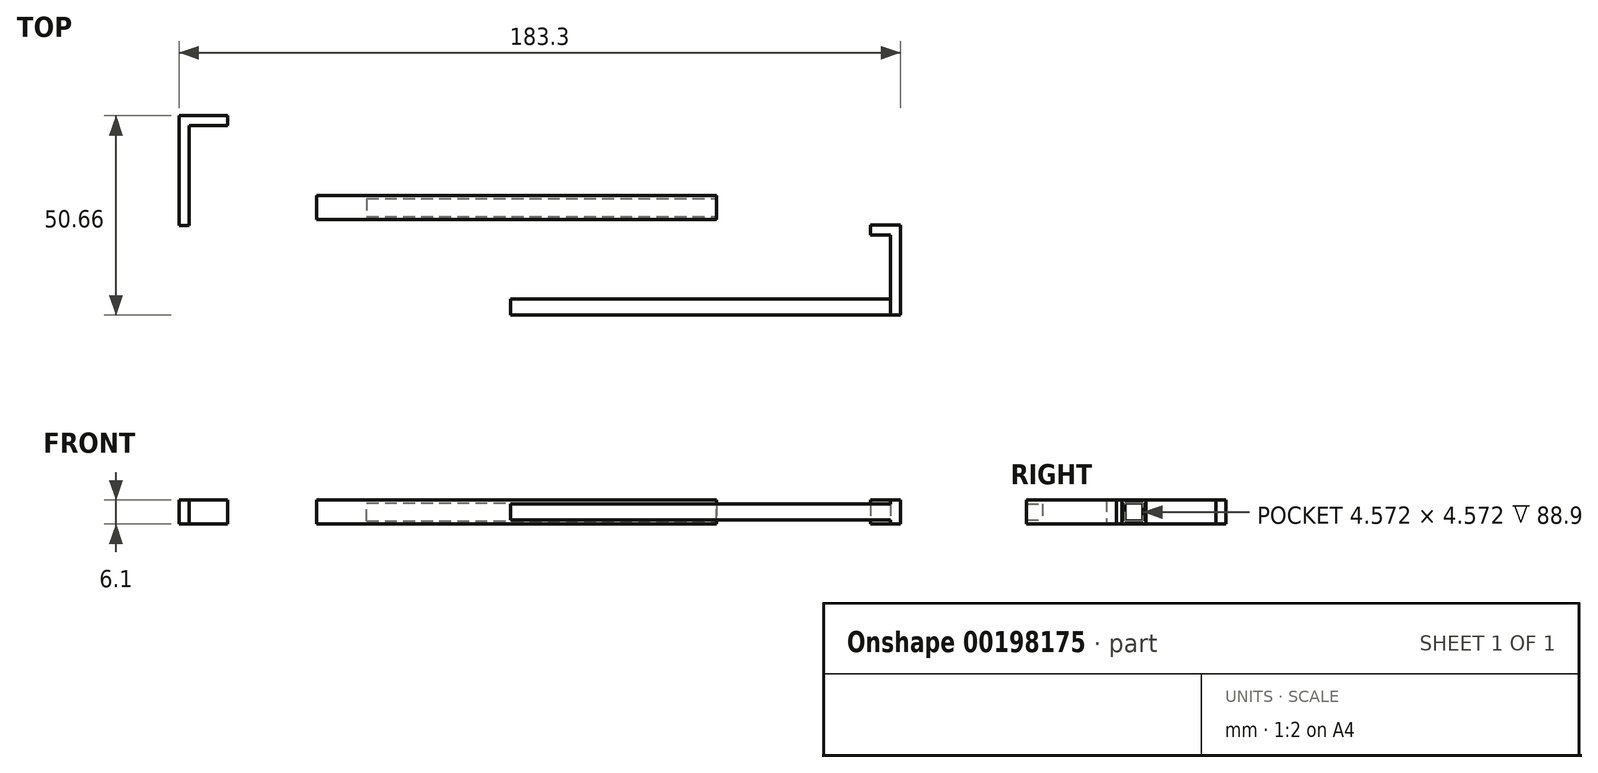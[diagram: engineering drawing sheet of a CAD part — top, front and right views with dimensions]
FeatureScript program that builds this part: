
annotation { "Feature Type Name" : "Feature", "Feature Type Description" : "" }
export const myFeature = defineFeature(function(context is Context, id is Id, definition is map)
    precondition{}
    {
        {
            var Q0;
            Q0=qCreatedBy(makeId("Top.planeOp"),FACE);
            var sketch = newSketch(context, id + "F0", { "sketchPlane" : qUnion([Q0])});
            skLineSegment(sketch, "E0", {"start": v(-26.88, 4.9) * mm, "end": v(-39.3, 4.9) * mm});
            skLineSegment(sketch, "E1", {"start": v(-39.3, 4.9) * mm, "end": v(-39.3, -23.03) * mm});
            skLineSegment(sketch, "E2", {"start": v(-39.3, -23.03) * mm, "end": v(-36.76, -23.03) * mm});
            skLineSegment(sketch, "E3", {"start": v(-36.76, -23.03) * mm, "end": v(-36.76, 2.37) * mm});
            skLineSegment(sketch, "E4", {"start": v(-36.76, 2.37) * mm, "end": v(-26.88, 2.37) * mm});
            skLineSegment(sketch, "E5", {"start": v(-26.88, 2.37) * mm, "end": v(-26.88, 4.9) * mm});
            skSolve(sketch);
        }
        {
            var Q0;
            Q0=qSketchRegion(id+"F0",true);
            extrude(context, id + "F1", {"entities" : qUnion([Q0]), "depth" : 6.1 * mm});
        }
        {
            var Q0;
            Q0=qCreatedBy(makeId("Top.planeOp"),FACE);
            var sketch = newSketch(context, id + "F2", { "sketchPlane" : qUnion([Q0])});
            skLineSegment(sketch, "E6.bottom", {"start": v(-4.27, -21.48) * mm, "end": v(97.33, -21.48) * mm});
            skLineSegment(sketch, "E6.top", {"start": v(-4.27, -15.39) * mm, "end": v(97.33, -15.39) * mm});
            skLineSegment(sketch, "E6.left", {"start": v(-4.27, -21.48) * mm, "end": v(-4.27, -15.39) * mm});
            skLineSegment(sketch, "E6.right", {"start": v(97.33, -21.48) * mm, "end": v(97.33, -15.39) * mm});
            skSolve(sketch);
        }
        {
            var Q0;
            Q0=qSketchRegion(id+"F2",true);
            extrude(context, id + "F3", {"entities" : qUnion([Q0]), "depth" : 6.1 * mm});
        }
        {
            var Q0;
            Q0=makeQuery(id+"F3.opExtrude","SWEPT_FACE",FACE,{"disambiguationData":[OSD([sQuery(id+"F2.wireOp",EDGE,"E6.right")])]});
            var sketch = newSketch(context, id + "F4", { "sketchPlane" : qUnion([Q0])});
            skLineSegment(sketch, "E7.bottom", {"start": v(-16.15, 0.76) * mm, "end": v(-20.72, 0.76) * mm});
            skLineSegment(sketch, "E7.top", {"start": v(-16.15, 5.33) * mm, "end": v(-20.72, 5.33) * mm});
            skLineSegment(sketch, "E7.left", {"start": v(-16.15, 0.76) * mm, "end": v(-16.15, 5.33) * mm});
            skLineSegment(sketch, "E7.right", {"start": v(-20.72, 0.76) * mm, "end": v(-20.72, 5.33) * mm});
            skPoint(sketch, "E7.middle", {"position": v(-18.44, 3.05) * mm});
            skPoint(sketch, "E7.middle.positionSnap0", {"position": v(-18.44, 6.1) * mm});
            skPoint(sketch, "E7.middle.positionSnap1", {"position": v(-15.39, 3.05) * mm});
            skPoint(sketch, "E7.centerSnap0", {"position": v(-18.44, 6.1) * mm});
            skPoint(sketch, "E7.centerSnap1", {"position": v(-15.39, 3.05) * mm});
            skSolve(sketch);
        }
        {
            var Q0;
            Q0=qSketchRegion(id+"F4",true);
            extrude(context, id + "F5", {"entities" : qUnion([Q0]), "operationType" : NewBodyOperationType.REMOVE, "oppositeDirection" : true, "depth" : 88.9 * mm});
        }
        {
            var Q0;
            Q0=qCreatedBy(makeId("Top.planeOp"),FACE);
            var sketch = newSketch(context, id + "F6", { "sketchPlane" : qUnion([Q0])});
            skLineSegment(sketch, "E8", {"start": v(141.46, -45.75) * mm, "end": v(141.46, -25.43) * mm});
            skLineSegment(sketch, "E9", {"start": v(141.46, -25.43) * mm, "end": v(136.38, -25.43) * mm});
            skLineSegment(sketch, "E10", {"start": v(136.38, -25.43) * mm, "end": v(136.38, -22.89) * mm});
            skLineSegment(sketch, "E11", {"start": v(136.38, -22.89) * mm, "end": v(144, -22.89) * mm});
            skLineSegment(sketch, "E12", {"start": v(144, -22.89) * mm, "end": v(144, -45.75) * mm});
            skLineSegment(sketch, "E13", {"start": v(144, -45.75) * mm, "end": v(141.46, -45.75) * mm});
            skSolve(sketch);
        }
        {
            var Q0;
            Q0=qSketchRegion(id+"F6",true);
            extrude(context, id + "F7", {"entities" : qUnion([Q0]), "depth" : 6.1 * mm});
        }
        {
            var Q0;
            Q0=makeQuery(id+"F7.opExtrude","SWEPT_FACE",FACE,{"disambiguationData":[OSD([sQuery(id+"F6.wireOp",EDGE,"E8")])]});
            var sketch = newSketch(context, id + "F8", { "sketchPlane" : qUnion([Q0])});
            skLineSegment(sketch, "E14.bottom", {"start": v(45.75, 5.08) * mm, "end": v(41.68, 5.08) * mm});
            skLineSegment(sketch, "E14.top", {"start": v(45.75, 1.02) * mm, "end": v(41.68, 1.02) * mm});
            skLineSegment(sketch, "E14.left", {"start": v(45.75, 5.08) * mm, "end": v(45.75, 1.02) * mm});
            skLineSegment(sketch, "E14.right", {"start": v(41.68, 5.08) * mm, "end": v(41.68, 1.02) * mm});
            skPoint(sketch, "E14.middle", {"position": v(43.72, 3.05) * mm});
            skPoint(sketch, "E14.middle.positionSnap0", {"position": v(45.75, 3.05) * mm});
            skPoint(sketch, "E14.centerSnap0", {"position": v(45.75, 3.05) * mm});
            skSolve(sketch);
        }
        {
            var Q0;
            Q0=qSketchRegion(id+"F8",true);
            extrude(context, id + "F9", {"entities" : qUnion([Q0]), "operationType" : NewBodyOperationType.ADD, "depth" : 96.52 * mm});
        }
    });
